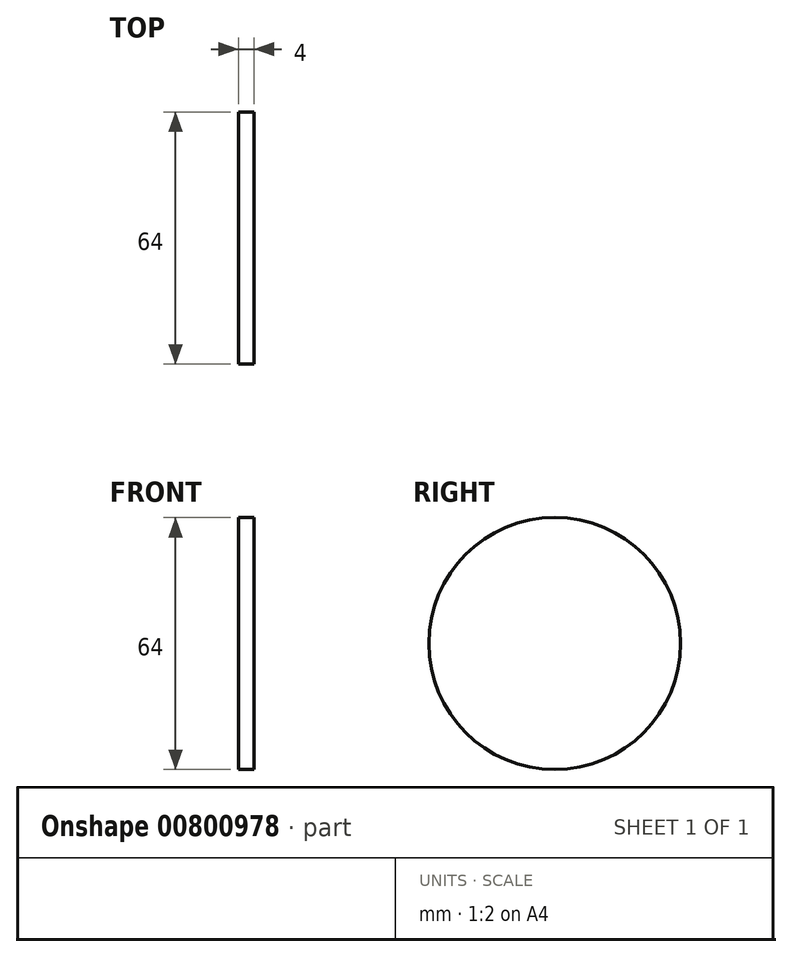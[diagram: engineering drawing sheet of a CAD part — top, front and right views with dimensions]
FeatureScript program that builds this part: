
annotation { "Feature Type Name" : "Feature", "Feature Type Description" : "" }
export const myFeature = defineFeature(function(context is Context, id is Id, definition is map)
    precondition{}
    {
        {
            var Q0;
            Q0=qCreatedBy(makeId("Top.planeOp"),FACE);
            var sketch = newSketch(context, id + "F0", { "sketchPlane" : qUnion([Q0])});
            skLineSegment(sketch, "E0.bottom", {"start": v(0, 0) * mm, "end": v(4, 0) * mm});
            skLineSegment(sketch, "E0.top", {"start": v(0, -32) * mm, "end": v(4, -32) * mm});
            skLineSegment(sketch, "E0.left", {"start": v(0, 0) * mm, "end": v(0, -32) * mm});
            skLineSegment(sketch, "E0.right", {"start": v(4, 0) * mm, "end": v(4, -32) * mm});
            skSolve(sketch);
        }
        {
            var Q0;
            Q0=makeQuery(id+"F0.imprint","IMPRINT",FACE,{"disambiguationData":[TD([[makeQuery(id+"F0.imprint","IMPRINT",EDGE,{"derivedFrom":sQuery(id+"F0.wireOp",EDGE,"E0.bottom")}),-1.0]])]});
            var Q1;
            Q1=sQuery(id+"F0.wireOp",EDGE,"E0.bottom");
            revolve(context, id + "F1", {"surfaceOperationType" : NewSurfaceOperationType.NEW, "entities" : qUnion([Q0]), "axis" : qUnion([Q1]), "revolveType" : RevolveType.FULL});
        }
    });
